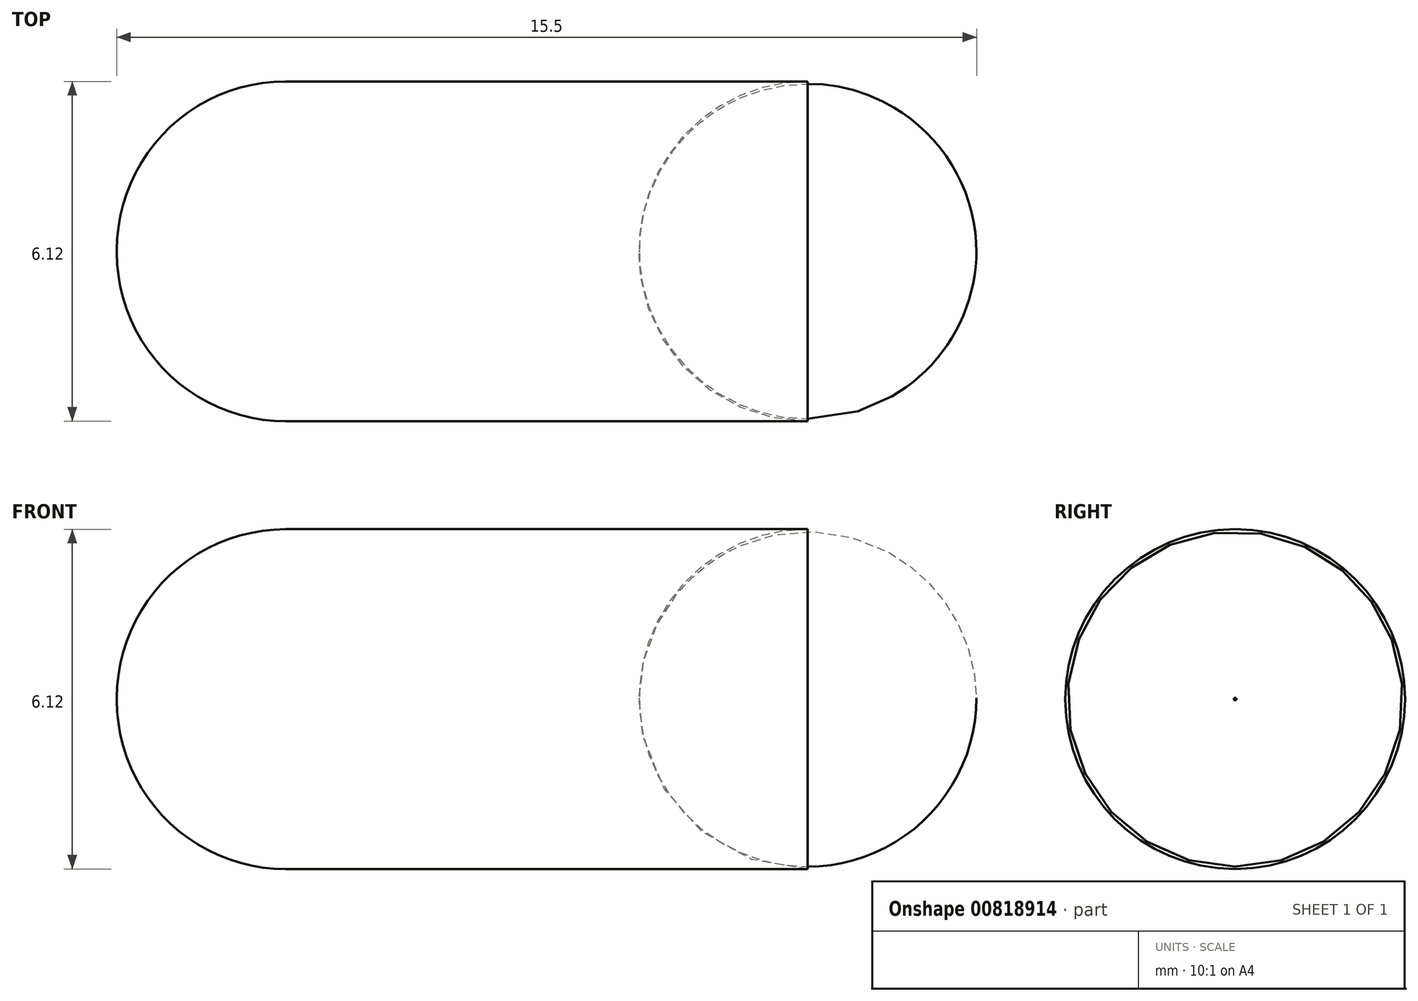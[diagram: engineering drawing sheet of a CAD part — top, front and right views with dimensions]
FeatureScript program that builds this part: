
annotation { "Feature Type Name" : "Feature", "Feature Type Description" : "" }
export const myFeature = defineFeature(function(context is Context, id is Id, definition is map)
    precondition{}
    {
        {
            var Q0;
            Q0=qCreatedBy(makeId("Front.planeOp"),FACE);
            var sketch = newSketch(context, id + "F0", { "sketchPlane" : qUnion([Q0])});
            skPoint(sketch, "E0.middle", {"position": v(0, 3.06) * mm});
            skLineSegment(sketch, "E1", {"start": v(-7.75, 0) * mm, "end": v(7.75, 0) * mm});
            skLineSegment(sketch, "E2", {"start": v(-7.75, 0) * mm, "end": v(-7.75, 0.02) * mm});
            skLineSegment(sketch, "E3", {"start": v(-4.7, 3.06) * mm, "end": v(4.7, 3.06) * mm});
            skLineSegment(sketch, "E4", {"start": v(7.75, 0.02) * mm, "end": v(7.75, 0) * mm});
            skPoint(sketch, "E5.visualSharp", {"position": v(-7.75, 3.06) * mm});
            skArc(sketch, "E5.filletArc", {"start": v(-4.7, 3.06) * mm, "mid": v(-6.86, 2.17) * mm, "end": v(-7.75, 0.02) * mm});
            skPoint(sketch, "E6.visualSharp", {"position": v(7.75, 3.06) * mm});
            skArc(sketch, "E6.filletArc", {"start": v(7.75, 0.02) * mm, "mid": v(6.86, 2.17) * mm, "end": v(4.7, 3.06) * mm});
            skSolve(sketch);
        }
        {
            var Q0;
            Q0=qSketchRegion(id+"F0",true);
            var Q1;
            Q1=sQuery(id+"F0.wireOp",EDGE,"E1");
            revolve(context, id + "F1", {"surfaceOperationType" : NewSurfaceOperationType.NEW, "entities" : qUnion([Q0]), "axis" : qUnion([Q1]), "revolveType" : RevolveType.FULL});
        }
    });
